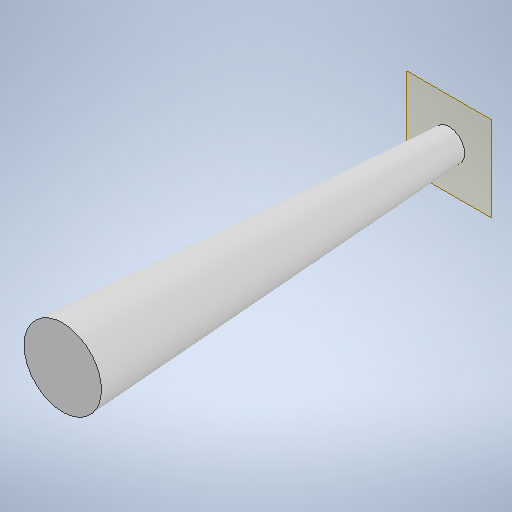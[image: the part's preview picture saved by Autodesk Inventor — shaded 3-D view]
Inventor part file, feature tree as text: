
AUTODESK INVENTOR PART (.ipt)
format: ipt  version: 2025.2 (Build 292293000, 293)  size: 246,272 bytes
history: native  units: mm
features: other x2, sketch x2, loft x1
ambient origin geometry x8: Origin, YZ Plane, XZ Plane, XY Plane, X Axis, Y Axis, Z Axis, Center Point
bodies: Body1 (feature_tree)
feature tree (5):
  other  "Sólido1"
  other  "Plano de trabalho1"
  loft  "Transição1"
  sketch  "Esboço1"  dims[d0=20.0mm d1=-100.0mm]
  sketch  "Esboço2"  dims[d2=8.0mm d3=0.0mm d4=90.0deg d5=0.0mm d6=90.0deg]
